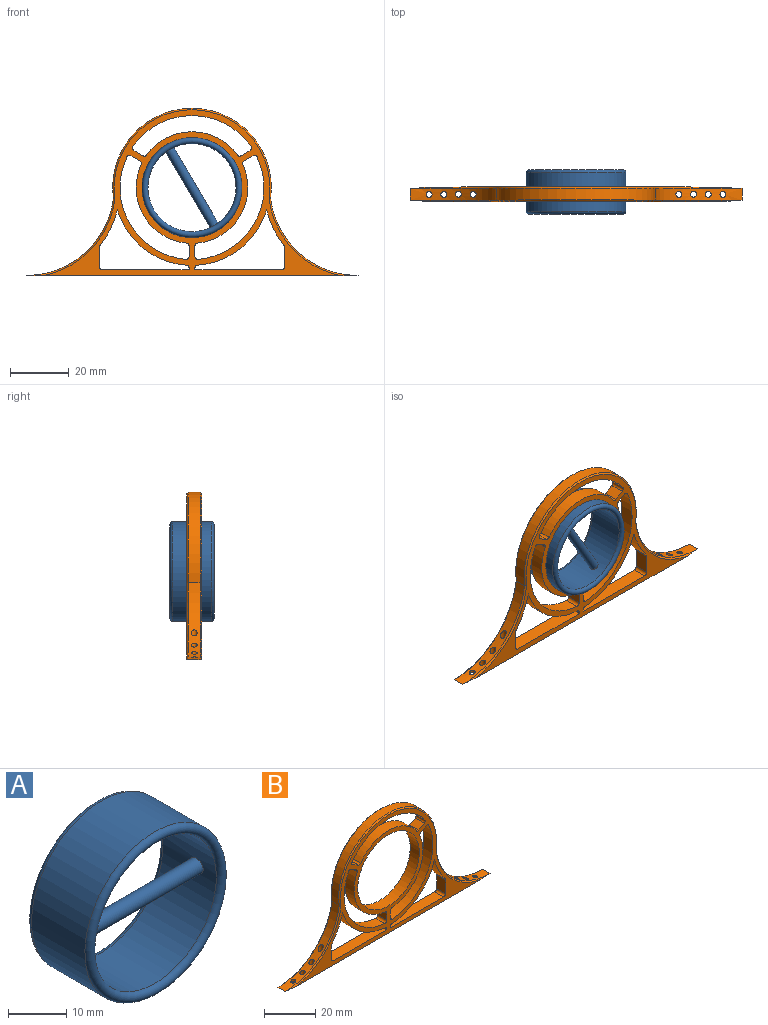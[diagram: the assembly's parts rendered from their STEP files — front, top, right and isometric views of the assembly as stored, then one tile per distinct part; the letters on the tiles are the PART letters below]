
ASSEMBLY  parts=2 mates=1
PART A: 5 faces, bbox 36.8x15x36.8 mm
  f0: cylinder r=15mm len=30mm, axis (0,1,0), area 1209.9mm2, adj f2,f3,f4
  f1: cylinder r=17mm len=34mm, axis (0,1,0), area 1388.6mm2, adj f2,f3
  f2: torus R=16mm, axis (0,-1,0), area 315.8mm2, adj f0,f1
  f3: torus R=16mm, axis (0,-1,0), area 315.8mm2, adj f0,f1
  f4: cylinder r=1.56mm len=30mm, axis (-1,0,0), area 293.4mm2, adj f0
PART B: 61 faces, bbox 113x5x57.5 mm
  f0: plane 102x56.5mm, normal (0,-1,0), area 927.7mm2, adj f11,f12,f14,f17,f18,f19,f20,f21
  f1: plane 102x56.5mm, normal (0,1,0), area 927.7mm2, adj f10,f12,f14,f17,f18,f19,f20,f21
  f2: cylinder r=1mm len=10.16mm, axis (0,0,1), area 57.2mm2, adj f5,f14
  f3: cylinder r=1mm len=5.63mm, axis (0,0,1), area 31.2mm2, adj f5,f14
  f4: cylinder r=1mm len=2.73mm, axis (0,0,1), area 14.5mm2, adj f5,f14
  f5: cylinder r=30mm len=29.76mm, axis (0,-1,0), area 158.5mm2, adj f2,f3,f4,f9,f14,f16,f59,f60
  f6: cylinder r=1mm len=10.16mm, axis (0,0,1), area 57.2mm2, adj f13,f14
  f7: cylinder r=1mm len=5.63mm, axis (0,0,1), area 31.2mm2, adj f13,f14
  f8: cylinder r=1mm len=2.73mm, axis (0,0,1), area 14.5mm2, adj f13,f14
  f9: cylinder r=27mm len=54mm, axis (0,1,0), area 369.5mm2, adj f5,f10,f11,f13
  f10: cone r=27mm half-angle=45deg, axis (0,-1,0), area 64.8mm2, adj f1,f9,f58,f59
  f11: cone r=26.5mm half-angle=45deg, axis (0,1,0), area 64.8mm2, adj f0,f9,f57,f60
  f12: cylinder r=17mm len=34mm, axis (0,1,0), area 534.1mm2, adj f0,f1
  f13: cylinder r=30mm len=29.76mm, axis (0,-1,0), area 158.6mm2, adj f6,f7,f8,f9,f14,f15,f57,f58
  f14: plane 113x5mm, normal (0,0,-1), area 532.5mm2, adj f0,f1,f2,f3,f4,f5,f6,f7
  f15: cylinder r=1mm len=2mm, axis (0,0,1), area 4.5mm2, adj f13,f14
  f16: cylinder r=1mm len=2mm, axis (0,0,1), area 4.5mm2, adj f5,f14
  f17: cylinder r=1mm len=5mm, axis (0,-1,0), area 8.3mm2, adj f0,f1,f18,f24
  f18: cylinder r=24.5mm len=34.81mm, axis (0,-1,0), area 235.7mm2, adj f0,f1,f17,f19
  f19: cylinder r=1mm len=5mm, axis (0,-1,0), area 8.3mm2, adj f0,f1,f18,f20
  f20: plane 5x3.04mm, normal (0.5,0,-0.87), area 17.6mm2, adj f0,f1,f19,f21
  f21: cylinder r=1mm len=5mm, axis (0,-1,0), area 7.4mm2, adj f0,f1,f20,f22
  f22: cylinder r=19mm len=26.71mm, axis (0,-1,0), area 179.9mm2, adj f0,f1,f21,f23
  f23: cylinder r=1mm len=5mm, axis (0,-1,0), area 7.4mm2, adj f0,f1,f22,f24
  f24: plane 5x3.52mm, normal (1,0,0), area 17.6mm2, adj f0,f1,f17,f23
  f25: cylinder r=1mm len=5mm, axis (0,-1,0), area 8.3mm2, adj f0,f1,f26,f32
  f26: cylinder r=24.5mm len=40.2mm, axis (0,-1,0), area 235.7mm2, adj f0,f1,f25,f27
  f27: cylinder r=1mm len=5mm, axis (0,-1,0), area 8.3mm2, adj f0,f1,f26,f28
  f28: plane 5x3.04mm, normal (0.5,0,0.87), area 17.6mm2, adj f0,f1,f27,f29
  f29: cylinder r=1mm len=5mm, axis (0,-1,0), area 7.4mm2, adj f0,f1,f28,f30
  f30: cylinder r=19mm len=30.84mm, axis (0,-1,0), area 179.9mm2, adj f0,f1,f29,f31
  f31: cylinder r=1mm len=5mm, axis (0,-1,0), area 7.4mm2, adj f0,f1,f30,f32
  f32: plane 5x3.04mm, normal (-0.5,0,0.87), area 17.6mm2, adj f0,f1,f25,f31
  f33: plane 5x3.52mm, normal (-1,0,0), area 17.6mm2, adj f0,f1,f34,f40
  f34: cylinder r=1mm len=5mm, axis (0,-1,0), area 7.4mm2, adj f0,f1,f33,f35
  f35: cylinder r=19mm len=26.71mm, axis (0,-1,0), area 179.9mm2, adj f0,f1,f34,f36
  f36: cylinder r=1mm len=5mm, axis (0,-1,0), area 7.4mm2, adj f0,f1,f35,f37
  f37: plane 5x3.04mm, normal (-0.5,0,-0.87), area 17.6mm2, adj f0,f1,f36,f38
  f38: cylinder r=1mm len=5mm, axis (0,-1,0), area 8.3mm2, adj f0,f1,f37,f39
  f39: cylinder r=24.5mm len=34.81mm, axis (0,-1,0), area 235.7mm2, adj f0,f1,f38,f40
  f40: cylinder r=1mm len=5mm, axis (0,-1,0), area 8.3mm2, adj f0,f1,f33,f39
  f41: plane 29.5x5mm, normal (0,0,1), area 147.5mm2, adj f0,f1,f42,f48
  f42: cylinder r=1mm len=5mm, axis (0,-1,0), area 7.9mm2, adj f0,f1,f41,f43
  f43: plane 6.68x5mm, normal (-1,0,0), area 33.4mm2, adj f0,f1,f42,f44
  f44: cylinder r=1mm len=5mm, axis (0,-1,0), area 3.3mm2, adj f0,f1,f43,f45
  f45: cylinder r=32mm len=12.16mm, axis (0,-1,0), area 68.1mm2, adj f0,f1,f44,f46
  f46: cylinder r=26.5mm len=23.48mm, axis (0,-1,0), area 160.2mm2, adj f0,f1,f45,f47
  f47: cylinder r=1mm len=5mm, axis (0,-1,0), area 7.5mm2, adj f0,f1,f46,f48
  f48: plane 5x0.57mm, normal (1,0,0), area 2.9mm2, adj f0,f1,f41,f47
  f49: cylinder r=1mm len=5mm, axis (0,-1,0), area 3.3mm2, adj f0,f1,f50,f56
  f50: plane 6.68x5mm, normal (1,0,0), area 33.4mm2, adj f0,f1,f49,f51
  f51: cylinder r=1mm len=5mm, axis (0,-1,0), area 7.9mm2, adj f0,f1,f50,f52
  f52: plane 29.5x5mm, normal (0,0,1), area 147.5mm2, adj f0,f1,f51,f53
  f53: plane 5x0.57mm, normal (-1,0,0), area 2.9mm2, adj f0,f1,f52,f54
  f54: cylinder r=1mm len=5mm, axis (0,-1,0), area 7.5mm2, adj f0,f1,f53,f55
  f55: cylinder r=26.5mm len=23.48mm, axis (0,-1,0), area 160.2mm2, adj f0,f1,f54,f56
  f56: cylinder r=32mm len=12.16mm, axis (0,-1,0), area 68.1mm2, adj f0,f1,f49,f55
  f57: cone r=30mm half-angle=45deg, axis (0,-1,0), area 28.3mm2, adj f0,f11,f13,f14
  f58: cone r=30.5mm half-angle=45deg, axis (0,1,0), area 28.3mm2, adj f1,f10,f13,f14
  f59: cone r=30mm half-angle=45deg, axis (0,1,0), area 28.3mm2, adj f1,f5,f10,f14
  f60: cone r=30.5mm half-angle=45deg, axis (0,-1,0), area 28.3mm2, adj f0,f5,f11,f14
PLACE A rot(axis=(0,1,0),59.6deg) t=(0,8.25,0)mm
PLACE B t=(0,2.5,0)mm
MATE cylindrical A.f1 <-> B.f12  axis (0,1,0) through (0,7.25,0)mm
